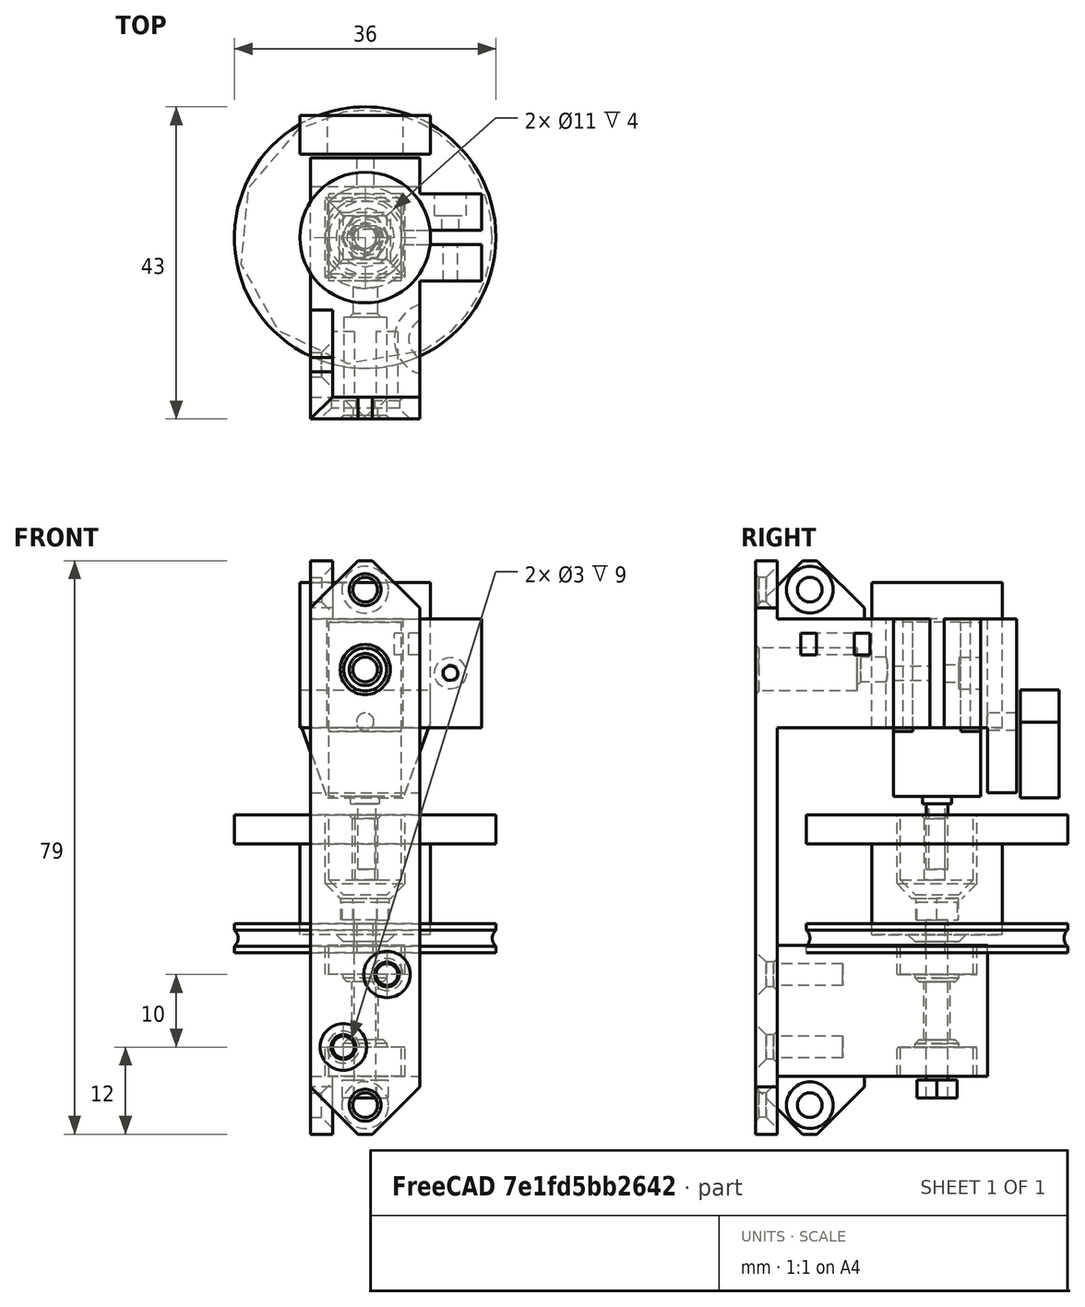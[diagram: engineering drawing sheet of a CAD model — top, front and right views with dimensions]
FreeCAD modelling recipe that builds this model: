
FCSTD DOCUMENT  (FreeCAD 0.18R16146 (Git))
Label: Motor and Opto Sensor Mount0.3
License: All rights reserved
LicenseURL: http://en.wikipedia.org/wiki/All_rights_reserved
objects: Part::Cylinder×35, Part::Cut×26, Part::Box×21, Part::Chamfer×16, Part::MultiFuse×15, Drawing::FeatureViewAnnotation×8, Part::Fuse×4, Part::Feature×3, Part::MultiCommon×2, Part::Mirroring×2, Part::Torus×1, Part::Cone×1, Drawing::FeaturePage×1
note: 126 computed .brp shape members not serialized (recipe doc carries the construction recipe); baked Part::Feature solids carry a one-line shape summary decoded from their .brp

FEATURE [Part::Box] Box406008004  label="gearbox004"
  AttacherType = Attacher::AttachEngine3D
  Height = 9
  Length = 12
  Placement = pos=(-6,-5,0) rot=(0,0,1;0rad)
  Width = 10
FEATURE [Part::Cylinder] Cylinder076  label="boss002"
  Angle = 360
  AttacherType = Attacher::AttachEngine3D
  Height = 1
  Placement = pos=(0,0,-1) rot=(0,0,1;0rad)
  Radius = 2
FEATURE [Part::Cylinder] Cylinder077
  Angle = 360
  AttacherType = Attacher::AttachEngine3D
  Height = 15
  Placement = pos=(0,0,9) rot=(0,0,1;0rad)
  Radius = 6
FEATURE [Part::Box] Box406008005  label="gearbox005"
  AttacherType = Attacher::AttachEngine3D
  Height = 27
  Length = 16
  Placement = pos=(-8,-5,0) rot=(0,0,1;0rad)
  Width = 10
FEATURE [Part::MultiCommon] Common001  label="motor002"
  Shapes = -> [Cylinder077,Box406008005]
FEATURE [Part::Cylinder] Cylinder078  label="shaft-002"
  Angle = 360
  AttacherType = Attacher::AttachEngine3D
  Height = 10
  Placement = pos=(0,0,-10) rot=(0,0,1;0rad)
  Radius = 1.5
FEATURE [Part::Box] Box406008006  label="Cube341"
  AttacherType = Attacher::AttachEngine3D
  Height = 12
  Length = 10
  Placement = pos=(-5,1,-11) rot=(0,0,1;0rad)
  Width = 10
FEATURE [Part::Cut] Cut001  label="shaft002"
  Base = -> Cylinder078
  Tool = -> Box406008006
FEATURE [Part::MultiFuse] Fusion103077013004017004  label="motor-assembled"
  Placement = pos=(0,0,20.5) rot=(0,0,1;1.5708rad)
  Shapes = -> [Box406008004,Cylinder076,Common001,Cut001]
FEATURE [Part::Cylinder] Cylinder028  label="Cylinder024"
  Angle = 360
  AttacherType = Attacher::AttachEngine3D
  Height = 10
  Placement = pos=(0,0,-1) rot=(0,0,1;0rad)
  Radius = 1.57
FEATURE [Part::Cylinder] Cylinder012  label="wheel1a"
  Angle = 360
  AttacherType = Attacher::AttachEngine3D
  Height = 4
  Radius = 18
FEATURE [Part::Box] Box084016  label="Cube067"
  AttacherType = Attacher::AttachEngine3D
  Height = 12
  Length = 10
  Placement = pos=(-5,1.1,-1.5) rot=(0,0,1;0rad)
  Width = 10
FEATURE [Part::Torus] Torus002
  Angle1 = -180
  Angle2 = 180
  Angle3 = 360
  AttacherType = Attacher::AttachEngine3D
  Placement = pos=(0,0,2) rot=(0,0,1;0rad)
  Radius1 = 19
  Radius2 = 1.5
FEATURE [Part::Cut] Cut057
  Base = -> Cylinder028
  Tool = -> Box084016
FEATURE [Part::Cut] Cut062
  Base = -> Cylinder012
  Tool = -> Cut057
FEATURE [Part::Cut] Cut063  label="wheel 0.1"
  Base = -> Cut062
  Placement = pos=(0,0,-1) rot=(0,0,1;0rad)
  Tool = -> Torus002
FEATURE [Part::Cylinder] Cylinder073  label="motor-bulge"
  Angle = 360
  AttacherType = Attacher::AttachEngine3D
  Height = 20
  Placement = pos=(0,0,30) rot=(0,0,1;0rad)
  Radius = 9
FEATURE [Part::Cylinder] Cylinder067
  Angle = 360
  AttacherType = Attacher::AttachEngine3D
  Height = 26
  Placement = pos=(0,0,20) rot=(0,0,1;0rad)
  Radius = 7
FEATURE [Part::Box] Box406017  label="gearbox001"
  AttacherType = Attacher::AttachEngine3D
  Height = 28
  Length = 16
  Placement = pos=(-8,-5.25,18) rot=(0,0,1;0rad)
  Width = 10.5
FEATURE [Part::MultiCommon] Common004  label="motor-hole"
  Placement = pos=(0,0,5) rot=(0,0,1;1.5708rad)
  Shapes = -> [Cylinder067,Box406017]
FEATURE [Part::Box] Box406016  label="clamp-slot"
  AttacherType = Attacher::AttachEngine3D
  Height = 32
  Length = 49
  Placement = pos=(48.48,1,22) rot=(0,0,1;3.14159rad)
  Width = 2
FEATURE [Part::Box] Box  label="Cube"
  AttacherType = Attacher::AttachEngine3D
  Height = 8
  Length = 15
  Placement = pos=(-7.5,-25,45) rot=(0,0,1;0rad)
  Width = 3
FEATURE [Part::Box] Box406008007  label="Cube342"
  AttacherType = Attacher::AttachEngine3D
  Height = 14.9
  Length = 18
  Placement = pos=(-9,13,34.3) rot=(0,0,1;0rad)
  Width = 5.3
FEATURE [Part::Cylinder] Cylinder079  label="Cylinder078"
  Angle = 360
  AttacherType = Attacher::AttachEngine3D
  Height = 17
  Placement = pos=(0,0,9) rot=(0,0,1;0rad)
  Radius = 1.75
FEATURE [Part::Box] Box406008008  label="Cube343"
  AttacherType = Attacher::AttachEngine3D
  Height = 19
  Length = 10
  Placement = pos=(-5,1.1,1.5) rot=(0,0,1;0rad)
  Width = 10
FEATURE [Part::Cut] Cut064  label="Motor Shaft Hole"
  Base = -> Cylinder079
  Tool = -> Box406008008
FEATURE [Part::Box] Box406008009  label="Cube344"
  AttacherType = Attacher::AttachEngine3D
  Height = 11
  Length = 10
  Placement = pos=(-5,-5,7) rot=(0,0,1;0rad)
  Width = 10
FEATURE [Part::Box] Box406008010  label="Cube345"
  AttacherType = Attacher::AttachEngine3D
  Height = 19.7
  Length = 17.5
  Placement = pos=(3.75,6,30.3) rot=(0,1,0;0.349066rad)
  Width = 13.3
FEATURE [Part::Box] Box406008011  label="Cube346"
  AttacherType = Attacher::AttachEngine3D
  Height = 19.7
  Length = 17.5
  Placement = pos=(3.75,6,30.3) rot=(0,1,0;0.349066rad)
  Width = 13.3
FEATURE [Part::Mirroring] Part__Mirroring  label="Cube346 (Mirror #1)"
  Base = (0,0,0)
  Normal = (1,0,0)
  Source = -> Box406008011
FEATURE [Part::MultiFuse] Fusion
  Shapes = -> [Box406008010,Part__Mirroring]
FEATURE [Part::Cut] Cut  label="Opto Sensor"
  Base = -> Box406008007
  Placement = pos=(0,-1.5,-14) rot=(0,0,1;0rad)
  Tool = -> Fusion
FEATURE [Part::Cut] Cut065  label="Square Peg"
  Base = -> Box406008009
  Tool = -> Cut064
FEATURE [Part::Box] Box406008012  label="Cube347"
  AttacherType = Attacher::AttachEngine3D
  Height = 11.5
  Length = 11
  Placement = pos=(-5.5,-5.5,6.5) rot=(0,0,1;0rad)
  Width = 11
FEATURE [Part::Cylinder] Cylinder
  Angle = 360
  AttacherType = Attacher::AttachEngine3D
  Height = 12.5
  Placement = pos=(0,0,1.5) rot=(0,0,1;0rad)
  Radius = 9
FEATURE [Part::Cylinder] Cylinder080  label="wheel1a001"
  Angle = 360
  AttacherType = Attacher::AttachEngine3D
  Height = 4
  Placement = pos=(0,0,14) rot=(0,0,1;0rad)
  Radius = 18
FEATURE [Part::Feature] Shape
  Placement = pos=(0,0,3.5) rot=(0,0,1;0rad)
  shape: bbox 6.697 x 5.8 x 15 mm, 8 faces (baked)
FEATURE [Part::MultiFuse] Fusion103077013004017005
  Shapes = -> [Cylinder080,Cylinder]
FEATURE [Part::Feature] Shape001
  Placement = pos=(0,0,3.5) rot=(0,0,1;0rad)
  shape: bbox 6.351 x 5.5 x 2.5 mm, 8 faces (baked)
FEATURE [Part::Cylinder] Cylinder081  label="Cylinder079"
  Angle = 360
  AttacherType = Attacher::AttachEngine3D
  Height = 25
  Placement = pos=(0,0,-21) rot=(0,0,1;0rad)
  Radius = 1.5
FEATURE [Part::MultiFuse] Fusion103077013004017006  label="M3 x 25 Hex Head"
  Shapes = -> [Shape001,Cylinder081]
FEATURE [Part::Cut] Cut066
  Base = -> Fusion103077013004017005
  Tool = -> Box406008012
FEATURE [Part::Cone] Cone
  Angle = 360
  AttacherType = Attacher::AttachEngine3D
  Height = 1
  Placement = pos=(0,0,0.5) rot=(0,0,1;0rad)
  Radius1 = 3
  Radius2 = 4
FEATURE [Part::MultiFuse] Fusion103077013004017007
  Shapes = -> [Cut066,Cone]
FEATURE [Part::Cut] Cut067
  Base = -> Fusion103077013004017007
  Tool = -> Shape
FEATURE [Part::Cylinder] Cylinder082  label="623 Bearing"
  Angle = 360
  AttacherType = Attacher::AttachEngine3D
  Height = 4
  Placement = pos=(0,0,-4) rot=(0,0,1;0rad)
  Radius = 5
FEATURE [Part::Cylinder] Cylinder083  label="623 Bearing001"
  Angle = 360
  AttacherType = Attacher::AttachEngine3D
  Height = 4
  Placement = pos=(0,0,-18) rot=(0,0,1;0rad)
  Radius = 5
FEATURE [Part::Feature] Shape002  label="Nylock"
  Placement = pos=(0,0,-21) rot=(0,0,1;0rad)
  shape: bbox 6.351 x 5.5 x 2.5 mm, 8 faces (baked)
FEATURE [Part::Cylinder] Cylinder084  label="Cylinder080"
  Angle = 360
  AttacherType = Attacher::AttachEngine3D
  Height = 6
  Placement = pos=(0,0,-2) rot=(0,0,1;0rad)
  Radius = 1.5
FEATURE [Part::Cut] Cut069
  Base = -> Cut067
  Tool = -> Cylinder084
FEATURE [Part::Cylinder] Cylinder085  label="Cylinder081"
  Angle = 360
  AttacherType = Attacher::AttachEngine3D
  Height = 12
  Placement = pos=(0,0,-14) rot=(0,0,1;0rad)
  Radius = 1.8
FEATURE [Part::Box] Box406008013  label="Cube348"
  AttacherType = Attacher::AttachEngine3D
  Height = 18
  Length = 15
  Placement = pos=(-7.5,-22,-18) rot=(0,0,1;0rad)
  Width = 29
FEATURE [Part::Cylinder] Cylinder086  label="623 Bearing002"
  Angle = 360
  AttacherType = Attacher::AttachEngine3D
  Height = 4
  Placement = pos=(0,0,-4) rot=(0,0,1;0rad)
  Radius = 5.5
FEATURE [Part::Cylinder] Cylinder087  label="623 Bearing003"
  Angle = 360
  AttacherType = Attacher::AttachEngine3D
  Height = 4
  Placement = pos=(0,0,-18) rot=(0,0,1;0rad)
  Radius = 5.5
FEATURE [Part::MultiFuse] Fusion103077013004017008  label="623 Bearing Holes"
  Shapes = -> [Cylinder086,Cylinder087]
FEATURE [Part::Cut] Cut070
  Base = -> Box406008013
  Tool = -> Fusion103077013004017008
FEATURE [Part::Cylinder] Cylinder088  label="Cylinder082"
  Angle = 360
  AttacherType = Attacher::AttachEngine3D
  Height = 1
  Placement = pos=(0,0,-5) rot=(0,0,1;0rad)
  Radius = 3
FEATURE [Part::Cylinder] Cylinder089  label="Cylinder083"
  Angle = 360
  AttacherType = Attacher::AttachEngine3D
  Height = 1
  Placement = pos=(0,0,-14) rot=(0,0,1;0rad)
  Radius = 3
FEATURE [Part::MultiFuse] Fusion103077013004017009
  Shapes = -> [Cylinder089,Cylinder088]
FEATURE [Part::Cut] Cut071
  Base = -> Cut070
  Tool = -> Fusion103077013004017009
FEATURE [Part::Cut] Cut072
  Base = -> Cut071
  Tool = -> Cylinder085
FEATURE [Part::Chamfer] Chamfer
  Base = -> Cut072
  Edges = 1 edges r=0.5: [Edge22]
FEATURE [Part::Chamfer] Chamfer001  label="Bearing Mount end"
  Base = -> Chamfer
  Edges = 1 edges r=0.5: [Edge16]
FEATURE [Part::Box] Box406008014  label="Cube349"
  AttacherType = Attacher::AttachEngine3D
  Height = 63
  Length = 15
  Placement = pos=(-7.5,-25,-18) rot=(0,0,1;0rad)
  Width = 3
FEATURE [Part::Box] Box406008015  label="Cube350"
  AttacherType = Attacher::AttachEngine3D
  Height = 15
  Length = 15
  Placement = pos=(-7.5,-22,35) rot=(0,0,1;0rad)
  Width = 31
FEATURE [Part::Cut] Cut073
  Base = -> Box406008015
  Tool = -> Common004
FEATURE [Part::Cylinder] Cylinder068
  Angle = 360
  AttacherType = Attacher::AttachEngine3D
  Height = 12
  Placement = pos=(11.75,0,42.5) rot=(0,0.707106,0.707107;3.14159rad)
  Radius = 1.2
FEATURE [Part::Cylinder] Cylinder069
  Angle = 360
  AttacherType = Attacher::AttachEngine3D
  Height = 12
  Placement = pos=(11.75,3,42.5) rot=(0,0.707106,0.707107;3.14159rad)
  Radius = 2.2
FEATURE [Part::MultiFuse] Fusion103077013  label="M2-screw001"
  Shapes = -> [Cylinder068,Cylinder069]
FEATURE [Part::Box] Box406008016  label="Cube351"
  AttacherType = Attacher::AttachEngine3D
  Height = 15
  Length = 9
  Placement = pos=(7,-6,35) rot=(0,0,1;0rad)
  Width = 12
FEATURE [Part::Fuse] Fusion103077013004017010
  Base = -> Cut073
  Tool = -> Box406008016
FEATURE [Part::Cut] Cut074
  Base = -> Fusion103077013004017010
  Tool = -> Box406016
FEATURE [Part::Box] Box406008017  label="Cube352"
  AttacherType = Attacher::AttachEngine3D
  Height = 24
  Length = 15
  Placement = pos=(-7.5,7,26) rot=(0,0,1;0rad)
  Width = 4
FEATURE [Part::Cylinder] Cylinder090  label="Cylinder084"
  Angle = 360
  AttacherType = Attacher::AttachEngine3D
  Height = 13
  Placement = pos=(0,16,35.8) rot=(1,0,0;1.5708rad)
  Radius = 1.2
FEATURE [Part::Cylinder] Cylinder091
  Angle = 360
  AttacherType = Attacher::AttachEngine3D
  Height = 12
  Placement = pos=(11.75,-12,42.5) rot=(0,0.707106,0.707107;3.14159rad)
  Radius = 1
FEATURE [Part::Fuse] Fusion103077013004017011
  Base = -> Fusion103077013
  Tool = -> Cylinder091
FEATURE [Part::Cut] Cut075
  Base = -> Cut074
  Tool = -> Fusion103077013004017011
FEATURE [Part::Fuse] Fusion103077013004017012
  Base = -> Box406008017
  Tool = -> Cut075
FEATURE [Part::Cut] Cut076  label="Motor Mount 0.2"
  Base = -> Fusion103077013004017012
  Placement = pos=(0,0,-5) rot=(0,0,1;0rad)
  Tool = -> Cylinder090
FEATURE [Part::Cylinder] Cylinder092
  Angle = 360
  AttacherType = Attacher::AttachEngine3D
  Height = 21
  Placement = pos=(-3,-13,-14) rot=(1,0,0;1.5708rad)
  Radius = 1.7
FEATURE [Part::Cylinder] Cylinder093
  Angle = 360
  AttacherType = Attacher::AttachEngine3D
  Height = 21
  Placement = pos=(3,-13,-4) rot=(1,0,0;1.5708rad)
  Radius = 1.7
FEATURE [Part::Cylinder] Cylinder094
  Angle = 360
  AttacherType = Attacher::AttachEngine3D
  Height = 21
  Placement = pos=(-3,-13,-14) rot=(1,0,0;1.5708rad)
  Radius = 1.5
FEATURE [Part::Cylinder] Cylinder095
  Angle = 360
  AttacherType = Attacher::AttachEngine3D
  Height = 21
  Placement = pos=(3,-13,-4) rot=(1,0,0;1.5708rad)
  Radius = 1.5
FEATURE [Part::MultiFuse] Fusion103077013004017013
  Shapes = -> [Cylinder092,Cylinder093]
FEATURE [Part::Cut] Cut077
  Base = -> Box406008014
  Tool = -> Fusion103077013004017013
FEATURE [Part::MultiFuse] Fusion103077013004017014
  Shapes = -> [Cylinder094,Cylinder095]
FEATURE [Part::Cut] Cut078  label="Bearing Mount End 0.2"
  Base = -> Chamfer001
  Tool = -> Fusion103077013004017014
FEATURE [Part::Cylinder] Cylinder096
  Angle = 360
  AttacherType = Attacher::AttachEngine3D
  Height = 21
  Placement = pos=(0,-13,49) rot=(1,0,0;1.5708rad)
  Radius = 1.7
FEATURE [Part::Cylinder] Cylinder097
  Angle = 360
  AttacherType = Attacher::AttachEngine3D
  Height = 21
  Placement = pos=(0,-13,-22) rot=(1,0,0;1.5708rad)
  Radius = 1.7
FEATURE [Part::Chamfer] Chamfer003  label="Wheel"
  Base = -> Cut069
  Edges = 4 edges r=2: [Edge11,Edge12,Edge15,Edge16]
FEATURE [Part::Chamfer] Chamfer004  label="Square Peg001"
  Base = -> Cut065
  Edges = 4 edges r=2: [Edge4,Edge5,Edge13,Edge15]
FEATURE [Part::Box] Box406008018  label="Cube353"
  AttacherType = Attacher::AttachEngine3D
  Height = 8
  Length = 15
  Placement = pos=(-7.5,-25,-26) rot=(0,0,1;0rad)
  Width = 3
FEATURE [Part::Cut] Cut079
  Base = -> Box406008018
  Tool = -> Cylinder097
FEATURE [Part::Cut] Cut080
  Base = -> Box
  Tool = -> Cylinder096
FEATURE [Part::MultiFuse] Fusion103077013004017015
  Shapes = -> [Cut079,Cut080]
FEATURE [Part::Chamfer] Chamfer005  label="Chamfer005 mount holes"
  Base = -> Fusion103077013004017015
  Edges = 2 edges r=1.5: [Edge13,Edge28]
FEATURE [Part::Chamfer] Chamfer006  label="Chamfer under side CS screw holes"
  Base = -> Cut077
  Edges = 2 edges r=1.5: [Edge8,Edge9]
FEATURE [Part::MultiFuse] Fusion103077013004017016
  Shapes = -> [Chamfer006,Chamfer005]
FEATURE [Part::Chamfer] Chamfer007  label="Chamfer Corner edges of mount"
  Base = -> Fusion103077013004017016
  Edges = 4 edges r=6.5: [Edge27,Edge29,Edge34,Edge39]
FEATURE [Part::Cylinder] Cylinder098
  Angle = 360
  AttacherType = Attacher::AttachEngine3D
  Height = 3
  Placement = pos=(-9,-9,36) rot=(1,0,0;0rad)
  Radius = 5
FEATURE [Part::Cylinder] Cylinder099
  Angle = 360
  AttacherType = Attacher::AttachEngine3D
  Height = 3
  Placement = pos=(-9,-9,36) rot=(1,0,0;0rad)
  Radius = 3
FEATURE [Part::Cut] Cut081  label="Cable tie Hole"
  Base = -> Cylinder098
  Placement = pos=(18,-5,4) rot=(0,0,1;0rad)
  Tool = -> Cylinder099
FEATURE [Part::Cut] Cut082
  Base = -> Cut076
  Tool = -> Cut081
FEATURE [Part::MultiFuse] Fusion103077013004017017
  Shapes = -> [Chamfer007,Cut082]
FEATURE [Drawing::FeatureViewAnnotation] Annotation
  Font = Sans
  Rotation = 0
  Scale = 7
  Text = Square Peg 0.1 - 0.2 Hole R 1.57 -> 1.75 and chamfered
  ViewResult = <g transform="translate(10,20) rotate(0)">\n<text id="Annotation"\n font-family="Sans"\n font-size="7"\n fill="#000000">\n<tspan x="0" dy="1em">Square Peg 0.1 - 0.2 Hole R 1.57 -> 1.75 and chamfered</tspan>\n</text>\n</g>
  Visible = true
  X = 10
  Y = 20
FEATURE [Part::Chamfer] Chamfer008  label="Square Peg 0.2"
  Base = -> Chamfer004
  Edges = 3 edges r=0.5: [Edge13,Edge14,Edge15]
FEATURE [Drawing::FeatureViewAnnotation] Annotation001
  Font = Sans
  Rotation = 0
  Scale = 7
  Text = Bearing Mount End 0.2 0 Hole R 1.5 -> 1.8
  ViewResult = <g transform="translate(10,60) rotate(0)">\n<text id="Annotation001"\n font-family="Sans"\n font-size="7"\n fill="#000000">\n<tspan x="0" dy="1em">Bearing Mount End 0.2 0 Hole R 1.5 -> 1.8</tspan>\n</text>\n</g>
  Visible = true
  X = 10
  Y = 60
FEATURE [Drawing::FeatureViewAnnotation] Annotation002
  Font = Sans
  Rotation = 0
  Scale = 7
  Text = Motor Mount Hole 6.25 -> 7mm
  ViewResult = <g transform="translate(10,40) rotate(0)">\n<text id="Annotation002"\n font-family="Sans"\n font-size="7"\n fill="#000000">\n<tspan x="0" dy="1em">Motor Mount Hole 6.25 -> 7mm</tspan>\n</text>\n</g>
  Visible = true
  X = 10
  Y = 40
FEATURE [Part::Chamfer] Chamfer009  label="Chamfer on bottom of mount holes (so they print better)"
  Base = -> Fusion103077013004017017
  Edges = 2 edges r=0.5: [Edge46,Edge47]
FEATURE [Part::Chamfer] Chamfer010  label="Motor and Opto Sensor Mount 0.2"
  Base = -> Chamfer009
  Edges = 2 edges r=0.5: [Edge102,Edge107]
FEATURE [Drawing::FeatureViewAnnotation] Annotation003
  Font = Sans
  Rotation = 0
  Scale = 7
  Text = Chamfered holes that are printed sideways
  ViewResult = <g transform="translate(10,80) rotate(0)">\n<text id="Annotation003"\n font-family="Sans"\n font-size="7"\n fill="#000000">\n<tspan x="0" dy="1em">Chamfered holes that are printed sideways</tspan>\n</text>\n</g>
  Visible = true
  X = 10
  Y = 80
FEATURE [Part::Cylinder] Cylinder100
  Angle = 360
  AttacherType = Attacher::AttachEngine3D
  Height = 28
  Placement = pos=(0,0,38) rot=(1,0,0;1.5708rad)
  Radius = 1.7
FEATURE [Drawing::FeatureViewAnnotation] Annotation004
  Font = Sans
  Rotation = 0
  Scale = 7
  Text = 0.2 -> 0.3 Changes
  ViewResult = <g transform="translate(10,100) rotate(0)">\n<text id="Annotation004"\n font-family="Sans"\n font-size="7"\n fill="#000000">\n<tspan x="0" dy="1em">0.2 -> 0.3 Changes</tspan>\n</text>\n</g>
  Visible = true
  X = 10
  Y = 100
FEATURE [Drawing::FeatureViewAnnotation] Annotation005
  Font = Sans
  Rotation = 0
  Scale = 7
  Text = Hole to hold motor
  ViewResult = <g transform="translate(20,120) rotate(0)">\n<text id="Annotation005"\n font-family="Sans"\n font-size="7"\n fill="#000000">\n<tspan x="0" dy="1em">Hole to hold motor</tspan>\n</text>\n</g>
  Visible = true
  X = 20
  Y = 120
FEATURE [Part::Cylinder] Cylinder101
  Angle = 360
  AttacherType = Attacher::AttachEngine3D
  Height = 20
  Placement = pos=(0,-11,38) rot=(1,0,0;1.5708rad)
  Radius = 2.95
FEATURE [Part::MultiFuse] Fusion103077013004017018
  Shapes = -> [Cylinder100,Cylinder101]
FEATURE [Part::Cylinder] Cylinder102
  Angle = 360
  AttacherType = Attacher::AttachEngine3D
  Height = 21
  Placement = pos=(-15,-17.5,-22) rot=(0,1,0;1.5708rad)
  Radius = 1.7
FEATURE [Part::Box] Box406008019  label="Cube354"
  AttacherType = Attacher::AttachEngine3D
  Height = 8
  Length = 15
  Placement = pos=(-4.5,-25,-26) rot=(0,0,1;1.5708rad)
  Width = 3
FEATURE [Part::Cut] Cut083
  Base = -> Box406008019
  Tool = -> Cylinder102
FEATURE [Part::Chamfer] Chamfer011  label="Chamfer Mount corner edges"
  Base = -> Cut083
  Edges = 2 edges r=6.5: [Edge4,Edge14]
FEATURE [Part::Chamfer] Chamfer012  label="Chamfer012 Mount Hole"
  Base = -> Chamfer011
  Edges = 1 edges r=1.5: [Edge10]
FEATURE [Part::Cylinder] Cylinder103
  Angle = 360
  AttacherType = Attacher::AttachEngine3D
  Height = 21
  Placement = pos=(-15,-17.5,-22) rot=(0,1,0;1.5708rad)
  Radius = 1.7
FEATURE [Part::Box] Box406008020  label="Cube355"
  AttacherType = Attacher::AttachEngine3D
  Height = 8
  Length = 15
  Placement = pos=(-4.5,-25,-26) rot=(0,0,1;1.5708rad)
  Width = 3
FEATURE [Part::Cut] Cut084
  Base = -> Box406008020
  Tool = -> Cylinder103
FEATURE [Part::Chamfer] Chamfer013  label="Chamfer Mount corner edges001"
  Base = -> Cut084
  Edges = 2 edges r=6.5: [Edge4,Edge14]
FEATURE [Part::Chamfer] Chamfer014  label="Chamfer012 Mount Hole001"
  Base = -> Chamfer013
  Edges = 1 edges r=1.5: [Edge10]
FEATURE [Part::Mirroring] Part__Mirroring001  label="Chamfer012 Mount Hole001 (Mirror #2)"
  Base = (0,0,0)
  Normal = (0,0,1)
  Placement = pos=(0,0,27) rot=(0,0,1;0rad)
  Source = -> Chamfer014
FEATURE [Drawing::FeatureViewAnnotation] Annotation006
  Font = Sans
  Rotation = 0
  Scale = 7
  Text = Additional mounts at 90 degrees
  ViewResult = <g transform="translate(20,140) rotate(0)">\n<text id="Annotation006"\n font-family="Sans"\n font-size="7"\n fill="#000000">\n<tspan x="0" dy="1em">Additional mounts at 90 degrees</tspan>\n</text>\n</g>
  Visible = true
  X = 20
  Y = 140
FEATURE [Drawing::FeatureViewAnnotation] Annotation007
  Font = Sans
  Rotation = 0
  Scale = 7
  Text = Switched Cable tie hole and offset
  ViewResult = <g transform="translate(20,160) rotate(0)">\n<text id="Annotation007"\n font-family="Sans"\n font-size="7"\n fill="#000000">\n<tspan x="0" dy="1em">Switched Cable tie hole and offset</tspan>\n</text>\n</g>
  Visible = true
  X = 20
  Y = 160
FEATURE [Drawing::FeaturePage] Page
  EditableTexts = AUTHOR NAME | CREATION DATE | SUPERVISOR NAME | CHECK DATE | SCALE | WEIGHT | NUMBER | SHEET | TITLE | SUBTITLE
  Group = -> [Annotation,Annotation001,Annotation002,Annotation003,Annotation004,Annotation005,Annotation006,Annotation007]
  Template = <path>
FEATURE [Part::Cut] Cut085
  Base = -> Chamfer010
  Tool = -> Fusion103077013004017018
FEATURE [Part::MultiFuse] Fusion103077013004017019
  Shapes = -> [Part__Mirroring001,Chamfer012]
FEATURE [Part::Fuse] Fusion103077013004017020
  Base = -> Cut085
  Tool = -> Fusion103077013004017019
FEATURE [Part::Chamfer] Chamfer015
  Base = -> Fusion103077013004017020
  Edges = 1 edges r=0.5: [Edge97]
FEATURE [Part::Chamfer] Chamfer016  label="Motor and Opto Sensor Mount 0.3"
  Base = -> Chamfer015
  Edges = 1 edges r=0.5: [Edge5]
note: 1 file-system path scrubbed to <path> (originals preserved in the JSON sidecar)
